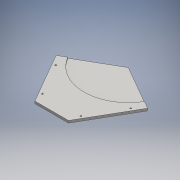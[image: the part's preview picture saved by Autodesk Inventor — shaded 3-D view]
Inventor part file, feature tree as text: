
AUTODESK INVENTOR PART (.ipt)
format: ipt  version: 2016 SP1 (Build 200210100, 210)  size: 136,192 bytes
history: native  units: mm
features: reference x3, extrude x2, sketch x2
ambient origin geometry x8: Origin, YZ Plane, XZ Plane, XY Plane, X Axis, Y Axis, Z Axis, Center Point
bodies: Solid1 (feature_tree)
feature tree (7):
  extrude  "Extrusion1"  Depth=5.0mm
  extrude  "Extrusion2"  Depth=5.0mm
  sketch  "Sketch1"  dims[d0=5.0mm d1=5.0mm]
  reference  "Reference2"
  reference  "Reference3"
  sketch  "Sketch2"  dims[d2=5.0mm d3=5.0mm d4=10.0mm d5=10.0mm d6=10.0mm d7=10.0mm d8=40.0mm d9=40.0mm d10=125.0mm d11=125.0mm d12=8.0mm d13=0.0mm d14=3.0mm d15=0.0mm]
  reference  "Reference4"
